# Revit family: Electronics_Community_Biamp_Dante-Amplified-Loudspeaker-Controllers_ALC-1604D
name_source: partatom
category: Communication Devices
units: mm (PartAtom-declared; Revit-internal decimal feet)

## family parameters
Cut with Voids When Loaded = No
Host = Face
Maintain Annotation Orientation = No
OmniClass Number = 23.85.10.11.14
OmniClass Title = Audio Equipment
Part Type = Normal
Room Calculation Point = No
Round Connector Dimension = Use Diameter
Shared = No

## types (1)
- ALC-1604D
    AC Mains Connector = IEC C20 inlet (20 A max) Region-specifc power cord provided
    AD Converters = 24-bit Tandem™ @ 48 kHz 125 dB(A) Dynamic Range - 0.005 % THD+N
    Ambient Operating Temperature = 0° - 45° C;  32° - 113° F
    Ambient Relative Humidity = 0-95% (non-condensing)
    Apparent Load = 840 VA
    Connector Description = 100-240 VAC, 50/60 Hz
    Crossover = Linear phase (FIR), Butterworth, Linkwitz-Riley, Bessel: 6 dB/oct to 48 dB/oct (IIR)
    Crosstalk (1 kHz) = -70 dB
    DA Converters = 24-bit Tandem™ @ 48 kHz 117 dB(A) Dynamic Range - 0.003 % THD+N
    Damping Control = Active DampingControl™ and LiveImpedance™ measurement
    Damping Factor = > 500 @ 8Ω, 20 Hz - 100 Hz
    Default Elevation = 1219 mm
    Delay = 2 s (input) + 100 ms (output) for signal alignment
    Depth = 373 mm  [stored 1.22375 ft]
    Description = Amplified Loudspeaker Controllers 4-Channel Units With DSP And Dante®
    Equalizer = Raised-cosine, custom FIR, parametric IIR:peaking, hi/lo-shelving, all-pass, band-pass, band-stop, hi/lo-pass
    Frequency Response = 20 Hz - 20 kHz ±0.5 dB, 1 W @ 8Ω
    Height = 44 mm  [stored 0.144357 ft]
    Housing Material = Biamp - Metal - Black
    IMD (from 0.1 W to Full Power) = < 0.05%
    Input Channels = Analog - 4;Dante - 4
    Input Impedance = 20 kΩ balanced
    Input Sens @8Ω = 26 dB - 4.91; 29 dB - 3.48; 32 dB - 2.46; 35 dB - 1.74
    Internal Precision = 32-bit foating point
    Latency = 2.5 ms fxed latency architecture
    Limiters = TruePower™, RMS voltage,RMS current, Peak limiter
    Manufacturer = Biamp
    Max Power Consumption = 840 W
    Maximum Input Level = 20 dBu
    Memory/Presets = 128 MB (RAM) plus 512 MB fash for presets
    Model = ALC-1604D
    Nominal Voltage (± 10%) = 100-240 V @ 50-60Hz
    Number of Poles = 1
    Operating Voltage = 60-264 V (with reduced power below 90 V)
    Output Channels = 4 Hi-Z or Lo-Z (bridgeable per ch. pair)
    Power Factor = 1
    Product Documentation Link = https://downloads.biamp.com
    Product Page URL = https://www.biamp.com
    Product data url = https://bimobject.com
    Remote Interface = ArmoníaPlus® System Manager
    Sample Rate Converter = 24-bit @ 44.1 kHz to 192 kHz 140 dB Dynamic Range - 0.0001 % THD+N
    Shipping Weight = 26.00 lb
    Signal-to-Noise Ratio 20 Hz- 20 kHz @ 8Ω = >110 dB(A)
    Slew Rate = > 50 V/ μs @ 8Ω, input flter bypassed
    Standards Compliance = Auto-sensing Fast Ethernet (IEEE 802.3u, 100 Mbit/s)
    Supported Topologies = Star
    THD+N (from 0.1 W to Full Power) = < 0.1% (typical < 0.05%)
    URL = https://www.biamp.com
    Version = 1
    Voltage = 240 V
    Weight = 17.30 lb
    Width = 442 mm  [stored 1.45013 ft]

note: [stored X ft] marks values corroborated as IEEE doubles in the binary element streams (Revit-internal decimal feet)

## geometry (parser evidence)
native form markers: Sweep x2
no freeform markers — native parametric forms only
